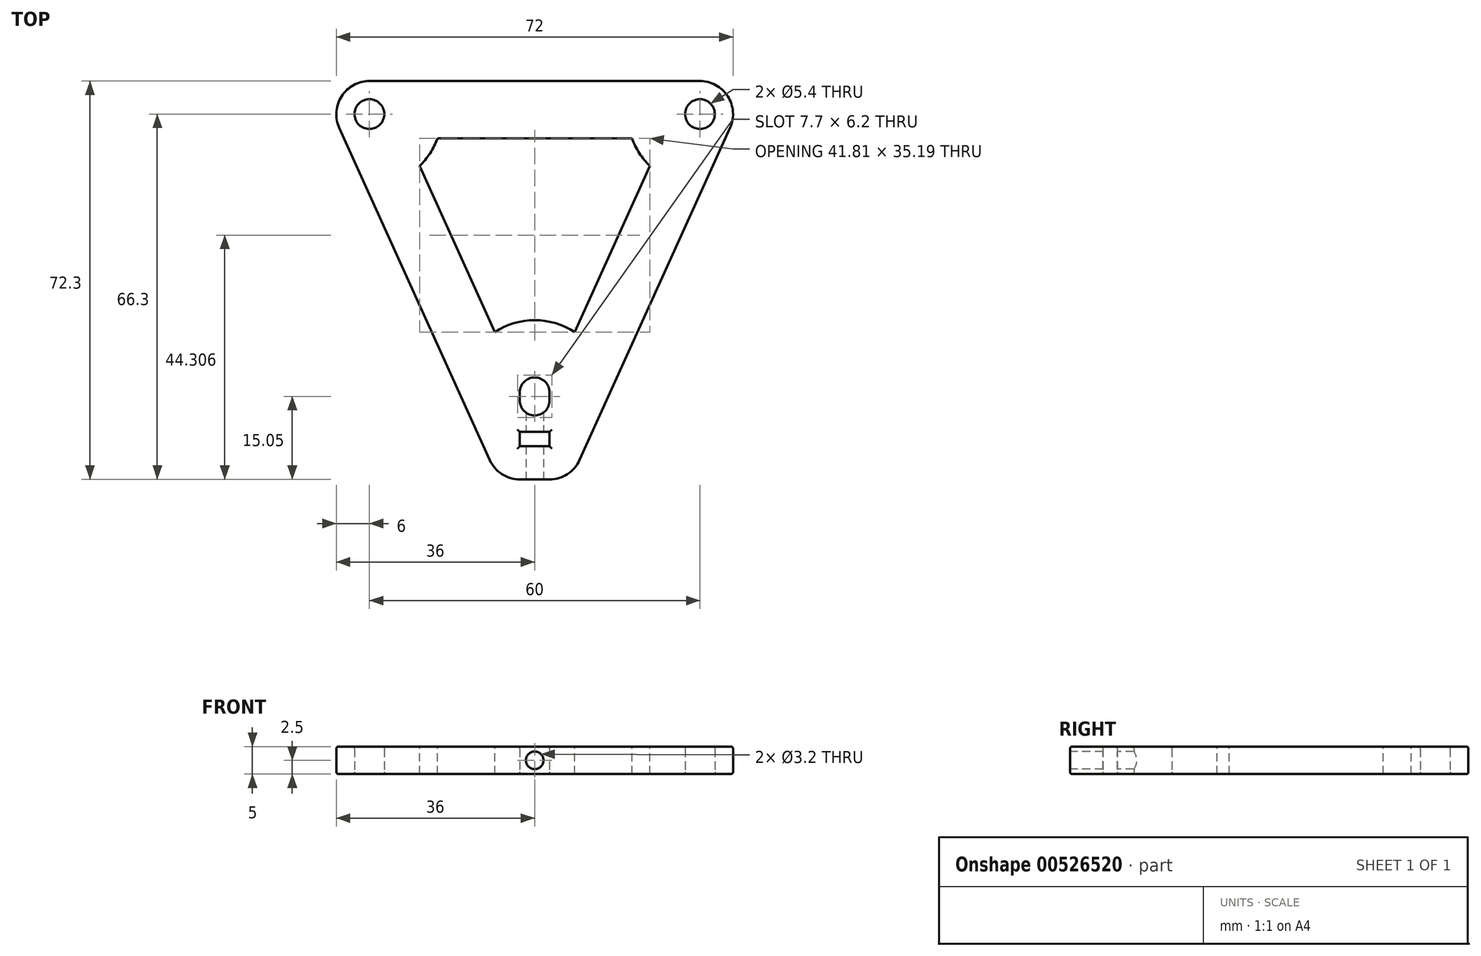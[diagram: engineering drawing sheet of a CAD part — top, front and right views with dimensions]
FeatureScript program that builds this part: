
annotation { "Feature Type Name" : "Feature", "Feature Type Description" : "" }
export const myFeature = defineFeature(function(context is Context, id is Id, definition is map)
    precondition{}
    {
        {
            var Q0;
            Q0=qCreatedBy(makeId("Top.planeOp"),FACE);
            var sketch = newSketch(context, id + "F0", { "sketchPlane" : qUnion([Q0])});
            skLineSegment(sketch, "E0", {"start": v(0, 26.9) * mm, "end": v(-30, 26.9) * mm});
            skLineSegment(sketch, "E1", {"start": v(0, -45.4) * mm, "end": v(0, -39.4) * mm});
            skLineSegment(sketch, "E2", {"start": v(0, -45.4) * mm, "end": v(-2.7, -45.4) * mm});
            skLineSegment(sketch, "E3", {"start": v(-8.17, -41.87) * mm, "end": v(-35.47, 18.43) * mm});
            skCircle(sketch, "E4", {"center": v(-30, 20.9) * mm, "radius": 2.7 * mm});
            skArc(sketch, "E5.0.startCap", {"start": v(0, -33.8) * mm, "mid": v(-1.9, -33) * mm, "end": v(-2.7, -31.1) * mm});
            skArc(sketch, "E5.0.endCap", {"start": v(-2.7, -29.6) * mm, "mid": v(-1.9, -27.7) * mm, "end": v(0, -26.9) * mm});
            skLineSegment(sketch, "E5.0.left", {"start": v(-2.7, -31.1) * mm, "end": v(-2.7, -29.6) * mm});
            skPoint(sketch, "E6.visualSharp", {"position": v(-39.3, 26.9) * mm});
            skArc(sketch, "E6.filletArc", {"start": v(-30, 26.9) * mm, "mid": v(-35.04, 24.15) * mm, "end": v(-35.47, 18.43) * mm});
            skPoint(sketch, "E7.visualSharp", {"position": v(-6.57, -45.4) * mm});
            skArc(sketch, "E7.filletArc", {"start": v(-8.17, -41.87) * mm, "mid": v(-5.95, -44.44) * mm, "end": v(-2.7, -45.4) * mm});
            skLineSegment(sketch, "E8.trimOffspring", {"start": v(0, -26.9) * mm, "end": v(0, 26.9) * mm});
            skLineSegment(sketch, "E9.bottom", {"start": v(0, -36.8) * mm, "end": v(-2.7, -36.8) * mm});
            skLineSegment(sketch, "E9.top", {"start": v(0, -39.4) * mm, "end": v(-2.7, -39.4) * mm});
            skLineSegment(sketch, "E9.right", {"start": v(-2.7, -36.8) * mm, "end": v(-2.7, -39.4) * mm});
            skLineSegment(sketch, "E10.trimOffspring", {"start": v(0, -36.8) * mm, "end": v(0, -33.8) * mm});
            skSolve(sketch);
        }
        {
            var Q0;
            Q0=makeQuery(id+"F0.imprint","IMPRINT",FACE,{"disambiguationData":[TD([[makeQuery(id+"F0.imprint","IMPRINT",EDGE,{"derivedFrom":sQuery(id+"F0.wireOp",EDGE,"E0")}),1.0]])]});
            extrude(context, id + "F1", {"entities" : qUnion([Q0]), "depth" : 5 * mm, "offsetDistance" : 25 * mm});
        }
        {
            var Q0;
            Q0=makeQuery(id+"F1.opExtrude","CAP_FACE",FACE,{"disambiguationData":[OSD([sQuery(id+"F0.wireOp",EDGE,"E0"),sQuery(id+"F0.wireOp",EDGE,"E1"),sQuery(id+"F0.wireOp",EDGE,"E2"),sQuery(id+"F0.wireOp",EDGE,"E3"),sQuery(id+"F0.wireOp",EDGE,"E4"),sQuery(id+"F0.wireOp",EDGE,"E5.0.startCap"),sQuery(id+"F0.wireOp",EDGE,"E5.0.endCap"),sQuery(id+"F0.wireOp",EDGE,"E5.0.left"),sQuery(id+"F0.wireOp",EDGE,"E6.filletArc"),sQuery(id+"F0.wireOp",EDGE,"E7.filletArc"),sQuery(id+"F0.wireOp",EDGE,"E8.trimOffspring"),sQuery(id+"F0.wireOp",EDGE,"E9.bottom"),sQuery(id+"F0.wireOp",EDGE,"E9.top"),sQuery(id+"F0.wireOp",EDGE,"E9.right"),sQuery(id+"F0.wireOp",EDGE,"E10.trimOffspring")])],"isStart":false});
            var sketch = newSketch(context, id + "F2", { "sketchPlane" : qUnion([Q0])});
            skLineSegment(sketch, "E11", {"start": v(0, 16.5) * mm, "end": v(-17.66, 16.5) * mm});
            skLineSegment(sketch, "E12", {"start": v(-20.9, 11.47) * mm, "end": v(-7.25, -18.69) * mm});
            skArc(sketch, "E13", {"start": v(0, -16.5) * mm, "mid": v(-3.79, -17.06) * mm, "end": v(-7.25, -18.69) * mm});
            skArc(sketch, "E14", {"start": v(-20.9, 11.47) * mm, "mid": v(-19, 13.8) * mm, "end": v(-17.66, 16.5) * mm});
            skLineSegment(sketch, "E15.trimOffspring", {"start": v(0, -16.5) * mm, "end": v(0, 16.5) * mm});
            skSolve(sketch);
        }
        {
            var Q0;
            Q0 = qSketchRegion(id + "F2", true);
            extrude(context, id + "F3", {"entities" : qUnion([Q0]), "operationType" : NewBodyOperationType.REMOVE, "endBound" : BoundingType.UP_TO_NEXT, "oppositeDirection" : true, "depth" : 25 * mm, "offsetDistance" : 25 * mm});
        }
        {
            var Q0;
            Q0=makeQuery(id+"F1.opExtrude","SWEPT_FACE",FACE,{"disambiguationData":[OSD([sQuery(id+"F0.wireOp",EDGE,"E2")])]});
            var sketch = newSketch(context, id + "F4", { "sketchPlane" : qUnion([Q0])});
            skCircle(sketch, "E16", {"center": v(0, 2.5) * mm, "radius": 1.6 * mm});
            skSolve(sketch);
        }
        {
            var Q0;
            Q0 = qSketchRegion(id + "F4", true);
            var Q1;
            Q1=makeQuery(id+"F1.opExtrude","SWEPT_FACE",FACE,{"disambiguationData":[OSD([sQuery(id+"F0.wireOp",EDGE,"E5.0.startCap")])]});
            extrude(context, id + "F5", {"entities" : qUnion([Q0]), "operationType" : NewBodyOperationType.REMOVE, "endBound" : BoundingType.UP_TO_SURFACE, "oppositeDirection" : true, "depth" : 25 * mm, "endBoundEntityFace" : qUnion([Q1]), "offsetDistance" : 25 * mm});
        }
        {
            var Q0;
            Q0=makeQuery(id+"F1.opExtrude","CAP_EDGE",EDGE,{"disambiguationData":[OSD([sQuery(id+"F0.wireOp",EDGE,"E3")])],"isStart":false});
            var Q1;
            Q1=makeQuery(id+"F1.opExtrude","CAP_EDGE",EDGE,{"disambiguationData":[OSD([sQuery(id+"F0.wireOp",EDGE,"E7.filletArc")])],"isStart":true});
            var Q2;
            Q2=makeQuery(id+"F5.boolean.opBoolean","COPY",EDGE,{"derivedFrom":makeQuery(id+"F5.opExtrude","CAP_EDGE",EDGE,{"disambiguationData":[OSD([sQuery(id+"F4.wireOp",EDGE,"E16")])],"isStart":true})});
            var Q3;
            Q3=makeQuery(id+"F1.opExtrude","CAP_EDGE",EDGE,{"disambiguationData":[OSD([sQuery(id+"F0.wireOp",EDGE,"E9.right")])],"isStart":false});
            var Q4;
            Q4=makeQuery(id+"F1.opExtrude","CAP_EDGE",EDGE,{"disambiguationData":[OSD([sQuery(id+"F0.wireOp",EDGE,"E9.top")])],"isStart":false});
            var Q5;
            Q5=makeQuery(id+"F1.opExtrude","CAP_EDGE",EDGE,{"disambiguationData":[OSD([sQuery(id+"F0.wireOp",EDGE,"E9.bottom")])],"isStart":false});
            var Q6;
            Q6=makeQuery(id+"F1.opExtrude","CAP_EDGE",EDGE,{"disambiguationData":[OSD([sQuery(id+"F0.wireOp",EDGE,"E9.top")])],"isStart":true});
            var Q7;
            Q7=makeQuery(id+"F1.opExtrude","CAP_EDGE",EDGE,{"disambiguationData":[OSD([sQuery(id+"F0.wireOp",EDGE,"E9.right")])],"isStart":true});
            var Q8;
            Q8=makeQuery(id+"F1.opExtrude","CAP_EDGE",EDGE,{"disambiguationData":[OSD([sQuery(id+"F0.wireOp",EDGE,"E9.bottom")])],"isStart":true});
            var Q9;
            Q9=makeQuery(id+"F1.opExtrude","CAP_EDGE",EDGE,{"disambiguationData":[OSD([sQuery(id+"F0.wireOp",EDGE,"E4")])],"isStart":false});
            var Q10;
            Q10=makeQuery(id+"F1.opExtrude","CAP_EDGE",EDGE,{"disambiguationData":[OSD([sQuery(id+"F0.wireOp",EDGE,"E4")])],"isStart":true});
            var Q11;
            Q11=makeQuery(id+"F1.opExtrude","CAP_EDGE",EDGE,{"disambiguationData":[OSD([sQuery(id+"F0.wireOp",EDGE,"E5.0.startCap")])],"isStart":true});
            var Q12;
            Q12=makeQuery(id+"F1.opExtrude","CAP_EDGE",EDGE,{"disambiguationData":[OSD([sQuery(id+"F0.wireOp",EDGE,"E5.0.left")])],"isStart":false});
            fillet(context, id + "F6", {"entities" : qUnion([Q0, Q1, Q2, Q3, Q4, Q5, Q6, Q7, Q8, Q9, Q10, Q11, Q12]), "radius" : 0.4 * mm, "tangentPropagation" : true, "allowEdgeOverflow" : false});
        }
        {
            var Q0;
            Q0=makeQuery(id+"F1.opExtrude","SWEPT_BODY",BODY,{"disambiguationData":[OSD([sQuery(id+"F0.wireOp",EDGE,"E0"),sQuery(id+"F0.wireOp",EDGE,"E1"),sQuery(id+"F0.wireOp",EDGE,"E2"),sQuery(id+"F0.wireOp",EDGE,"E3"),sQuery(id+"F0.wireOp",EDGE,"E4"),sQuery(id+"F0.wireOp",EDGE,"E5.0.startCap"),sQuery(id+"F0.wireOp",EDGE,"E5.0.endCap"),sQuery(id+"F0.wireOp",EDGE,"E5.0.left"),sQuery(id+"F0.wireOp",EDGE,"E6.filletArc"),sQuery(id+"F0.wireOp",EDGE,"E7.filletArc"),sQuery(id+"F0.wireOp",EDGE,"E8.trimOffspring"),sQuery(id+"F0.wireOp",EDGE,"E9.bottom"),sQuery(id+"F0.wireOp",EDGE,"E9.top"),sQuery(id+"F0.wireOp",EDGE,"E9.right"),sQuery(id+"F0.wireOp",EDGE,"E10.trimOffspring")])]});
            var Q1;
            {var subQ0=sQuery(id+"F0.wireOp",EDGE,"E0");var subQ5=sQuery(id+"F0.wireOp",EDGE,"E8.trimOffspring");Q1=makeQuery(id+"F3.boolean.opBoolean","SPLIT",FACE,{"disambiguationData":[TD([makeQuery(id+"F1.opExtrude","SWEPT_FACE",FACE,{"disambiguationData":[OSD([subQ0])]})])],"derivedFrom":makeQuery(id+"F1.opExtrude","SWEPT_FACE",FACE,{"disambiguationData":[OSD([subQ5])]})});}
            mirror(context, id + "F7", {"operationType" : NewBodyOperationType.ADD, "entities" : qUnion([Q0]), "mirrorPlane" : qUnion([Q1])});
        }
    });
